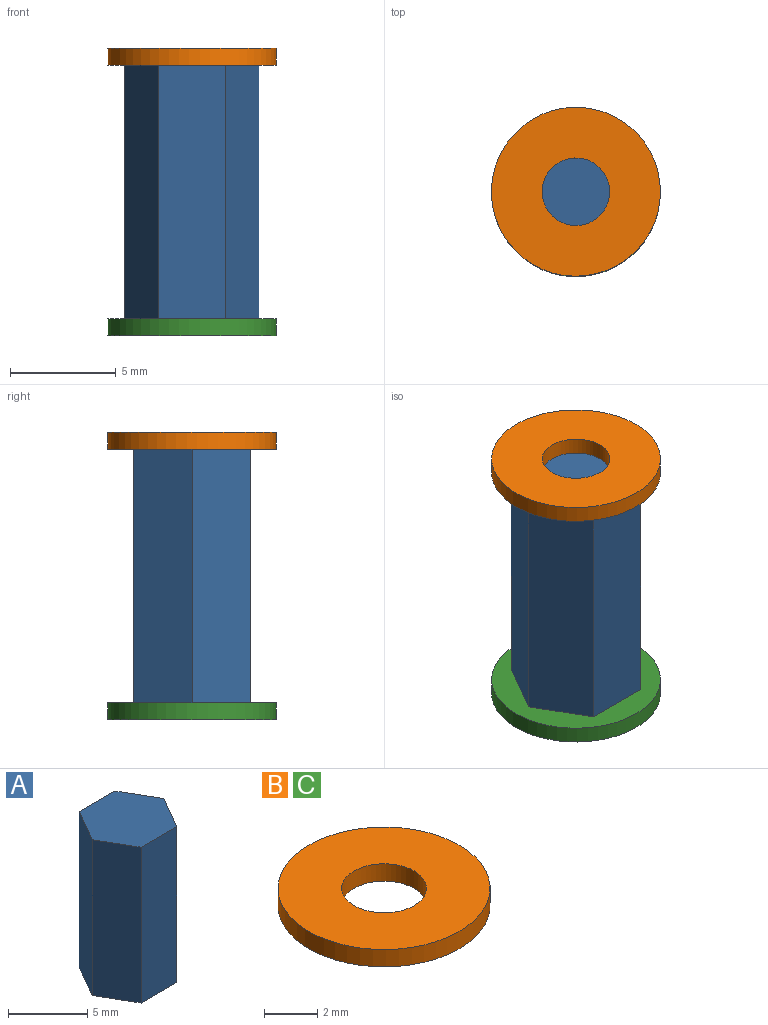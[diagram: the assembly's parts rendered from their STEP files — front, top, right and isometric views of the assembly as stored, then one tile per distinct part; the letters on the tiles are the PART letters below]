
ASSEMBLY  parts=3 mates=4
PART A: 8 faces, bbox 6.4x5.5x12 mm
  f0: plane 12x2.75mm, normal (-0.87,-0.5,0), area 38.1mm2, adj f1,f5,f6,f7
  f1: plane 12x3.18mm, normal (0,-1,0), area 38.1mm2, adj f0,f2,f6,f7
  f2: plane 12x2.75mm, normal (0.87,-0.5,0), area 38.1mm2, adj f1,f3,f6,f7
  f3: plane 12x2.75mm, normal (0.87,0.5,0), area 38.1mm2, adj f2,f4,f6,f7
  f4: plane 12x3.18mm, normal (0,1,0), area 38.1mm2, adj f3,f5,f6,f7
  f5: plane 12x2.75mm, normal (-0.87,0.5,0), area 38.1mm2, adj f0,f4,f6,f7
  f6: plane 6.35x5.5mm, normal (0,0,1), area 26.2mm2, adj f0,f1,f2,f3,f4,f5
  f7: plane 6.35x5.5mm, normal (0,0,-1), area 26.2mm2, adj f0,f1,f2,f3,f4,f5
PART B: 4 faces, bbox 8x8x0.8 mm
  f0: cylinder r=4mm len=8mm, axis (0,0,-1), area 20.1mm2, adj f1,f2
  f1: plane 8x8mm, normal (0,0,1), area 42.2mm2, adj f0,f3
  f2: plane 8x8mm, normal (0,0,-1), area 42.2mm2, adj f0,f3
  f3: cylinder r=1.6mm len=3.2mm, axis (0,0,1), area 8mm2, adj f1,f2
PART C: same geometry as B
PLACE A t=(-17.46,3.13,30.35)mm
PLACE B t=(-17.46,3.13,36.75)mm
PLACE C t=(-17.46,3.13,23.95)mm
MATE cylindrical A.f6 <-> B.f0  axis (0,0,1) through (-17.46,3.13,36.35)mm
MATE planar A.f6 <-> B.f0  axis (0,0,1) through (-17.46,3.13,36.35)mm
MATE planar A.f7 <-> C.f0  axis (0,0,-1) through (-17.46,3.13,24.35)mm
MATE cylindrical C.f0 <-> B.f0  axis (0,0,1) through (-17.46,3.13,24.35)mm
